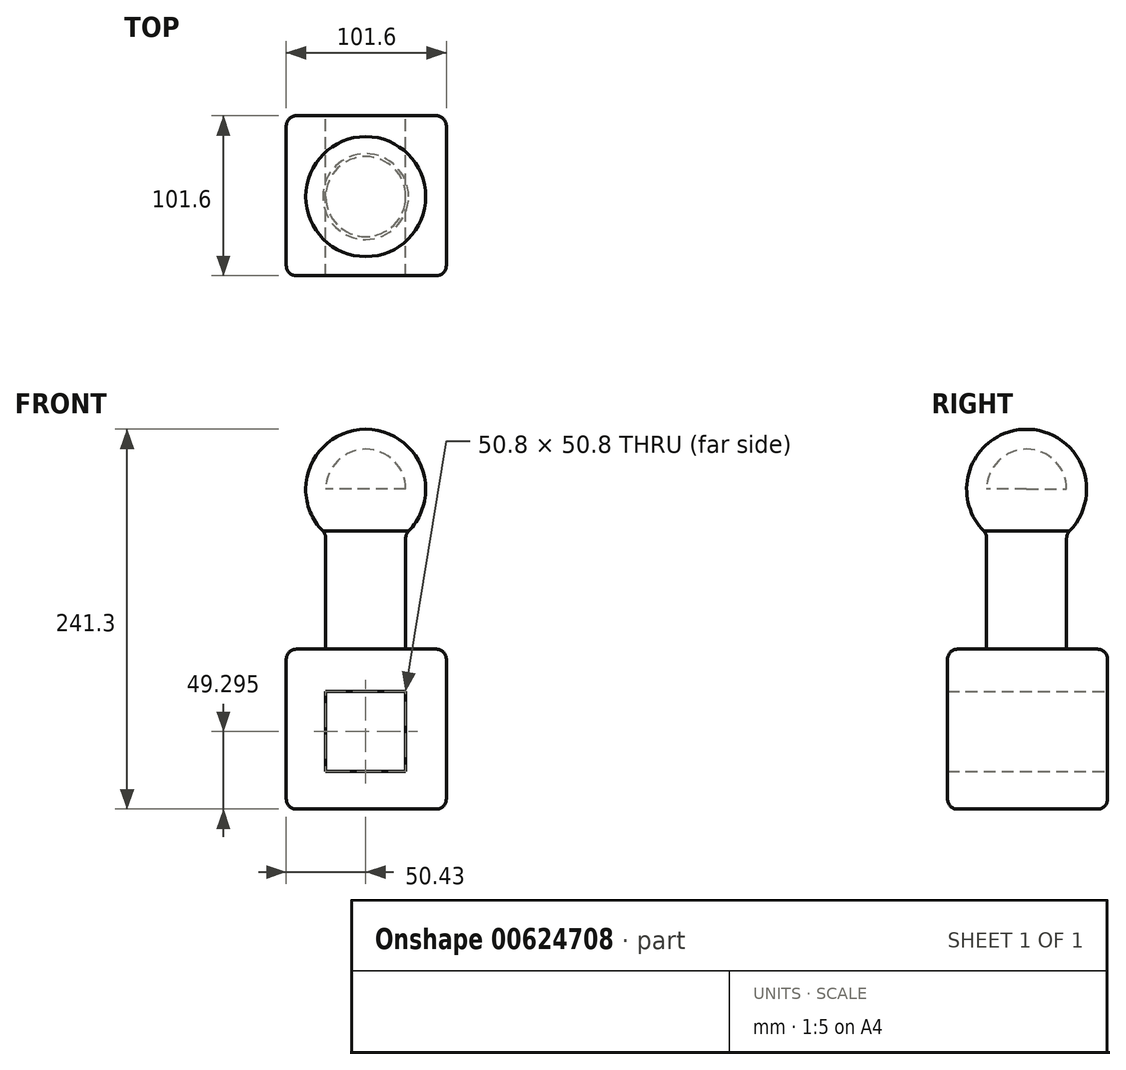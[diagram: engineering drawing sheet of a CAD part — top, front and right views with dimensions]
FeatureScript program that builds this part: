
annotation { "Feature Type Name" : "Feature", "Feature Type Description" : "" }
export const myFeature = defineFeature(function(context is Context, id is Id, definition is map)
    precondition{}
    {
        {
            var Q0;
            Q0=qCreatedBy(makeId("Top.planeOp"),FACE);
            var sketch = newSketch(context, id + "F0", { "sketchPlane" : qUnion([Q0])});
            skLineSegment(sketch, "E0.bottom", {"start": v(-50.43, 51.34) * mm, "end": v(51.17, 51.34) * mm});
            skLineSegment(sketch, "E0.top", {"start": v(-50.43, -50.26) * mm, "end": v(51.17, -50.26) * mm});
            skLineSegment(sketch, "E0.left", {"start": v(-50.43, 51.34) * mm, "end": v(-50.43, -50.26) * mm});
            skLineSegment(sketch, "E0.right", {"start": v(51.17, 51.34) * mm, "end": v(51.17, -50.26) * mm});
            skSolve(sketch);
        }
        {
            var Q0;
            Q0=makeQuery(id+"F0.imprint","IMPRINT",FACE,{"disambiguationData":[TD([[makeQuery(id+"F0.imprint","IMPRINT",EDGE,{"derivedFrom":sQuery(id+"F0.wireOp",EDGE,"E0.bottom")}),-1.0]])]});
            extrude(context, id + "F1", {"entities" : qUnion([Q0]), "depth" : 101.6 * mm, "offsetDistance" : 25.4 * mm});
        }
        {
            var Q0;
            Q0=makeQuery(id+"F1.opExtrude","CAP_FACE",FACE,{"disambiguationData":[OSD([sQuery(id+"F0.wireOp",EDGE,"E0.bottom"),sQuery(id+"F0.wireOp",EDGE,"E0.top"),sQuery(id+"F0.wireOp",EDGE,"E0.left"),sQuery(id+"F0.wireOp",EDGE,"E0.right")])],"isStart":false});
            var sketch = newSketch(context, id + "F2", { "sketchPlane" : qUnion([Q0])});
            skCircle(sketch, "E1", {"center": v(0, 0) * mm, "radius": 25.4 * mm});
            skSolve(sketch);
        }
        {
            var Q0;
            Q0=makeQuery(id+"F2.imprint","IMPRINT",FACE,{"disambiguationData":[TD([[makeQuery(id+"F2.imprint","IMPRINT",EDGE,{"derivedFrom":sQuery(id+"F2.wireOp",EDGE,"E1")}),1.0]])]});
            extrude(context, id + "F3", {"entities" : qUnion([Q0]), "operationType" : NewBodyOperationType.ADD, "depth" : 101.6 * mm, "offsetDistance" : 25.4 * mm});
        }
        {
            var Q0;
            Q0=makeQuery(id+"F3.opExtrude","CAP_FACE",FACE,{"disambiguationData":[OSD([sQuery(id+"F2.wireOp",EDGE,"E1")])],"isStart":false});
            var sketch = newSketch(context, id + "F4", { "sketchPlane" : qUnion([Q0])});
            skCircle(sketch, "E2", {"center": v(0, 0) * mm, "radius": 38.1 * mm});
            skLineSegment(sketch, "E3", {"start": v(-38.1, 0) * mm, "end": v(38.1, 0) * mm});
            skSolve(sketch);
        }
        {
            var Q0;
            {var subQ0=sQuery(id+"F4.wireOp",EDGE,"E3");var subQ1=sQuery(id+"F4.wireOp",EDGE,"E2");var subQ2=makeQuery(id+"F4.imprint","INTERSECT",VERTEX,{"disambiguationData":[OD(0.0)],"derivedFrom":[subQ1,subQ0]});Q0=makeQuery(id+"F4.imprint","IMPRINT",FACE,{"disambiguationData":[TD([[makeQuery(id+"F4.imprint","IMPRINT",EDGE,{"disambiguationData":[TD([[subQ2,-1.0]])],"derivedFrom":subQ1}),1.0]])]});}
            var Q1;
            Q1=sQuery(id+"F4.wireOp",EDGE,"E3");
            revolve(context, id + "F5", {"operationType" : NewBodyOperationType.ADD, "entities" : qUnion([Q0]), "axis" : qUnion([Q1]), "revolveType" : RevolveType.FULL});
        }
        {
            var Q0;
            Q0=makeQuery(id+"F1.opExtrude","SWEPT_FACE",FACE,{"disambiguationData":[OSD([sQuery(id+"F0.wireOp",EDGE,"E0.bottom")])]});
            var sketch = newSketch(context, id + "F6", { "sketchPlane" : qUnion([Q0])});
            skLineSegment(sketch, "E4.bottom", {"start": v(25.4, 74.7) * mm, "end": v(-25.4, 74.7) * mm});
            skLineSegment(sketch, "E4.top", {"start": v(25.4, 23.9) * mm, "end": v(-25.4, 23.9) * mm});
            skLineSegment(sketch, "E4.left", {"start": v(25.4, 74.7) * mm, "end": v(25.4, 23.9) * mm});
            skLineSegment(sketch, "E4.right", {"start": v(-25.4, 74.7) * mm, "end": v(-25.4, 23.9) * mm});
            skPoint(sketch, "E4.middle", {"position": v(0, 49.3) * mm});
            skSolve(sketch);
        }
        {
            var Q0;
            Q0=makeQuery(id+"F6.imprint","IMPRINT",FACE,{"disambiguationData":[TD([[makeQuery(id+"F6.imprint","IMPRINT",EDGE,{"derivedFrom":sQuery(id+"F6.wireOp",EDGE,"E4.bottom")}),1.0]])]});
            extrude(context, id + "F7", {"entities" : qUnion([Q0]), "operationType" : NewBodyOperationType.REMOVE, "oppositeDirection" : true, "depth" : 101.6 * mm, "offsetDistance" : 25.4 * mm});
        }
        {
            var Q0;
            Q0=makeQuery(id+"F1.opExtrude","CAP_EDGE",EDGE,{"disambiguationData":[OSD([sQuery(id+"F0.wireOp",EDGE,"E0.right")])],"isStart":false});
            var Q1;
            Q1=makeQuery(id+"F1.opExtrude","CAP_EDGE",EDGE,{"disambiguationData":[OSD([sQuery(id+"F0.wireOp",EDGE,"E0.bottom")])],"isStart":false});
            var Q2;
            Q2=makeQuery(id+"F1.opExtrude","SWEPT_FACE",FACE,{"disambiguationData":[OSD([sQuery(id+"F0.wireOp",EDGE,"E0.right")])]});
            var Q3;
            Q3=makeQuery(id+"F1.opExtrude","SWEPT_EDGE",EDGE,{"disambiguationData":[OSD([sQuery(id+"F0.wireOp",EDGE,"E0.bottom"),sQuery(id+"F0.wireOp",EDGE,"E0.right")])]});
            var Q4;
            Q4=makeQuery(id+"F1.opExtrude","CAP_EDGE",EDGE,{"disambiguationData":[OSD([sQuery(id+"F0.wireOp",EDGE,"E0.bottom")])],"isStart":true});
            var Q5;
            Q5=makeQuery(id+"F1.opExtrude","SWEPT_EDGE",EDGE,{"disambiguationData":[OSD([sQuery(id+"F0.wireOp",EDGE,"E0.bottom"),sQuery(id+"F0.wireOp",EDGE,"E0.left")])]});
            var Q6;
            Q6=makeQuery(id+"F5.boolean.opBoolean","INTERSECT",EDGE,{"derivedFrom":[makeQuery(id+"F3.opExtrude","SWEPT_FACE",FACE,{"disambiguationData":[OSD([sQuery(id+"F2.wireOp",EDGE,"E1")])]}),makeQuery(id+"F5.opRevolve","SWEPT_FACE",FACE,{"disambiguationData":[OSD([sQuery(id+"F4.wireOp",EDGE,"E2")])]})]});
            var Q7;
            Q7=makeQuery(id+"F3.opExtrude","CAP_EDGE",EDGE,{"disambiguationData":[OSD([sQuery(id+"F2.wireOp",EDGE,"E1")])],"isStart":true});
            var Q8;
            Q8=makeQuery(id+"F1.opExtrude","CAP_EDGE",EDGE,{"disambiguationData":[OSD([sQuery(id+"F0.wireOp",EDGE,"E0.top")])],"isStart":false});
            var Q9;
            Q9=makeQuery(id+"F1.opExtrude","SWEPT_EDGE",EDGE,{"disambiguationData":[OSD([sQuery(id+"F0.wireOp",EDGE,"E0.top"),sQuery(id+"F0.wireOp",EDGE,"E0.left")])]});
            var Q10;
            Q10=makeQuery(id+"F1.opExtrude","CAP_EDGE",EDGE,{"disambiguationData":[OSD([sQuery(id+"F0.wireOp",EDGE,"E0.top")])],"isStart":true});
            var Q11;
            Q11=makeQuery(id+"F1.opExtrude","SWEPT_EDGE",EDGE,{"disambiguationData":[OSD([sQuery(id+"F0.wireOp",EDGE,"E0.top"),sQuery(id+"F0.wireOp",EDGE,"E0.right")])]});
            var Q12;
            Q12=makeQuery(id+"F1.opExtrude","CAP_EDGE",EDGE,{"disambiguationData":[OSD([sQuery(id+"F0.wireOp",EDGE,"E0.left")])],"isStart":false});
            var Q13;
            Q13=makeQuery(id+"F1.opExtrude","CAP_EDGE",EDGE,{"disambiguationData":[OSD([sQuery(id+"F0.wireOp",EDGE,"E0.left")])],"isStart":true});
            fillet(context, id + "F8", {"entities" : qUnion([Q0, Q1, Q2, Q3, Q4, Q5, Q6, Q7, Q8, Q9, Q10, Q11, Q12, Q13]), "radius" : 6.35 * mm, "tangentPropagation" : true, "allowEdgeOverflow" : false});
        }
    });
